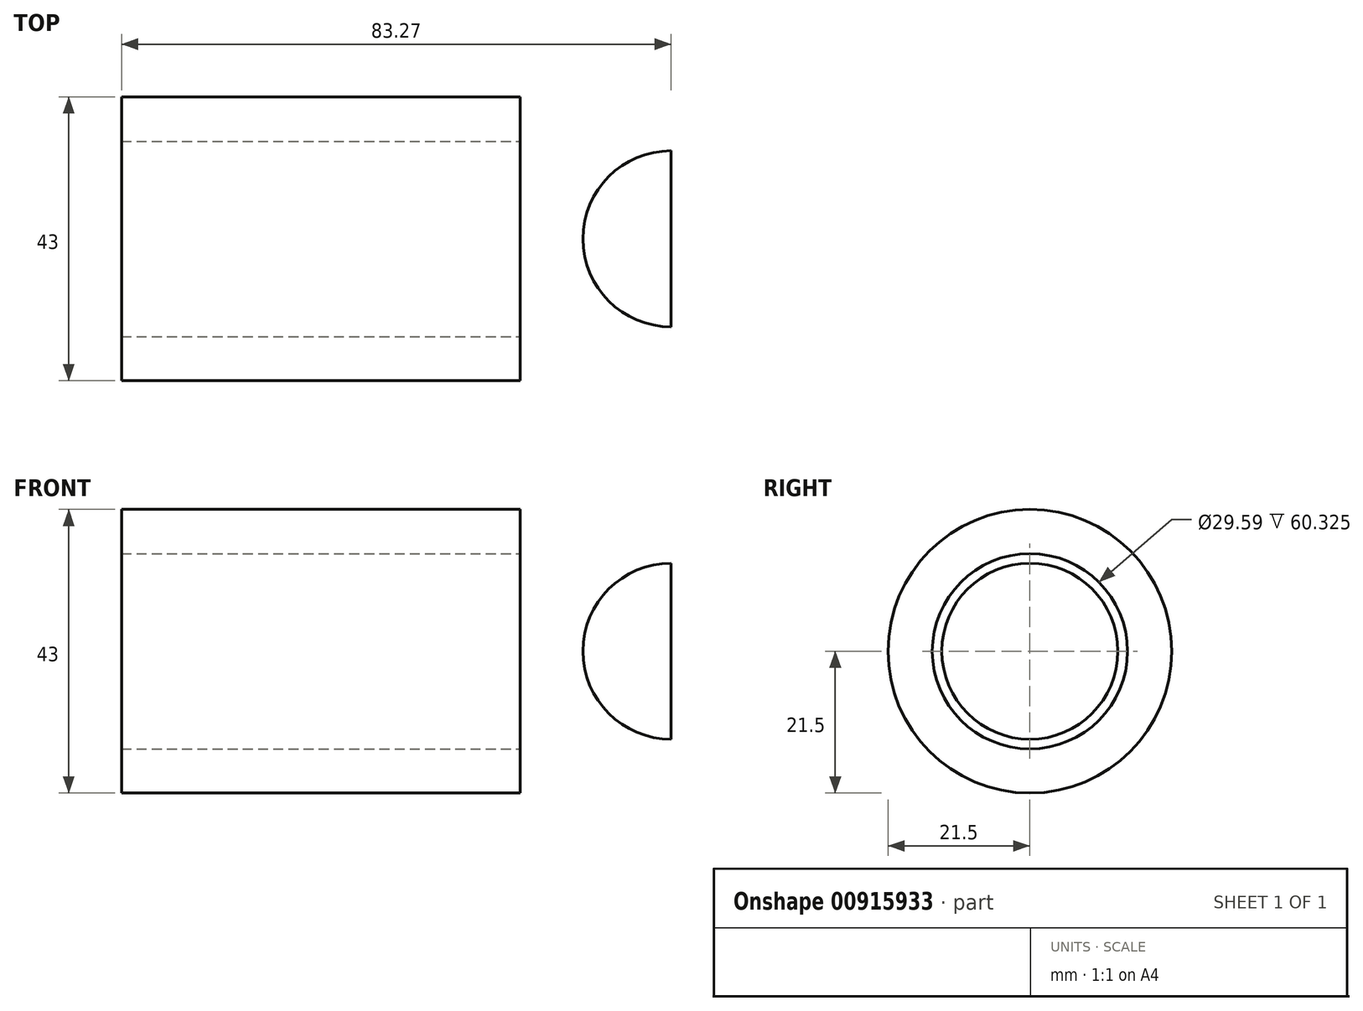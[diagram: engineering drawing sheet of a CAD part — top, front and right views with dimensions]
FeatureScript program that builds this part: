
annotation { "Feature Type Name" : "Feature", "Feature Type Description" : "" }
export const myFeature = defineFeature(function(context is Context, id is Id, definition is map)
    precondition{}
    {
        {
            var Q0;
            Q0=qCreatedBy(makeId("Front.planeOp"),FACE);
            var sketch = newSketch(context, id + "F0", { "sketchPlane" : qUnion([Q0])});
            skArc(sketch, "E0", {"start": v(0, 13.34) * mm, "mid": v(-13.34, 0) * mm, "end": v(0, -13.34) * mm});
            skLineSegment(sketch, "E1", {"start": v(0, 13.34) * mm, "end": v(0, -13.34) * mm});
            skPoint(sketch, "E2.orphan", {"position": v(0, 16.5) * mm});
            skSolve(sketch);
        }
        {
            var Q0;
            Q0=makeQuery(id+"F0.imprint","IMPRINT",FACE,{"disambiguationData":[TD([[makeQuery(id+"F0.imprint","IMPRINT",EDGE,{"derivedFrom":sQuery(id+"F0.wireOp",EDGE,"E0")}),1.0]])]});
            var Q1;
            Q1=sQuery(id+"F0.wireOp",EDGE,"E1");
            revolve(context, id + "F1", {"surfaceOperationType" : NewSurfaceOperationType.NEW, "entities" : qUnion([Q0]), "axis" : qUnion([Q1]), "revolveType" : RevolveType.TWO_DIRECTIONS, "angle" : 90 * degree, "angleBack" : 270 * degree});
        }
        {
            var Q0;
            Q0=qCreatedBy(makeId("Front.planeOp"),FACE);
            var sketch = newSketch(context, id + "F2", { "sketchPlane" : qUnion([Q0])});
            skLineSegment(sketch, "E3.bottom", {"start": v(-22.95, 14.8) * mm, "end": v(-83.27, 14.8) * mm});
            skLineSegment(sketch, "E3.left", {"start": v(-22.95, 14.8) * mm, "end": v(-22.95, 0) * mm, "construction": true});
            skLineSegment(sketch, "E3.right", {"start": v(-83.27, 14.8) * mm, "end": v(-83.27, 0) * mm, "construction": true});
            skLineSegment(sketch, "E4", {"start": v(-22.95, 0) * mm, "end": v(-83.27, 0) * mm, "construction": true});
            skLineSegment(sketch, "E5", {"start": v(-83.27, 14.8) * mm, "end": v(-83.27, 21.5) * mm});
            skLineSegment(sketch, "E6", {"start": v(-83.27, 21.5) * mm, "end": v(-22.84, 21.5) * mm});
            skLineSegment(sketch, "E7", {"start": v(-22.84, 21.5) * mm, "end": v(-22.95, 14.8) * mm});
            skSolve(sketch);
        }
        {
            var Q0;
            Q0=makeQuery(id+"F2.imprint","IMPRINT",FACE,{"disambiguationData":[TD([[makeQuery(id+"F2.imprint","IMPRINT",EDGE,{"derivedFrom":sQuery(id+"F2.wireOp",EDGE,"E3.bottom")}),-1.0]])]});
            var Q1;
            Q1=sQuery(id+"F2.wireOp",EDGE,"E6");
            var Q2;
            Q2=sQuery(id+"F2.wireOp",EDGE,"E7");
            var Q3;
            Q3=sQuery(id+"F2.wireOp",EDGE,"E3.bottom");
            var Q4;
            Q4=sQuery(id+"F2.wireOp",EDGE,"E5");
            var Q5;
            Q5=sQuery(id+"F2.wireOp",EDGE,"E4");
            revolve(context, id + "F3", {"surfaceOperationType" : NewSurfaceOperationType.NEW, "entities" : qUnion([Q0]), "surfaceEntities" : qUnion([Q1, Q2, Q3, Q4]), "axis" : qUnion([Q5]), "revolveType" : RevolveType.FULL});
        }
    });
